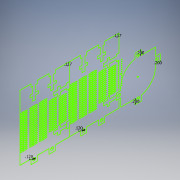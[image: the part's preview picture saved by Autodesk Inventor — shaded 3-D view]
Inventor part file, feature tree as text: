
AUTODESK INVENTOR PART (.ipt)
format: ipt  version: 2016 (Build 200138000, 138)  size: 222,720 bytes
history: native  units: in
note: dims shown in document units (in); Inventor stores cm internally (conversion verified against a paired STEP export)
features: sketch x1
ambient origin geometry x8: Origin, YZ Plane, XZ Plane, XY Plane, X Axis, Y Axis, Z Axis, Center Point
feature tree (1):
  sketch  "Sketch1"  dims[d30=0.12in d36=0.117in d67=0.12in d68=0.117in d73=0.2in d74=0.2in d75=0.2in]
